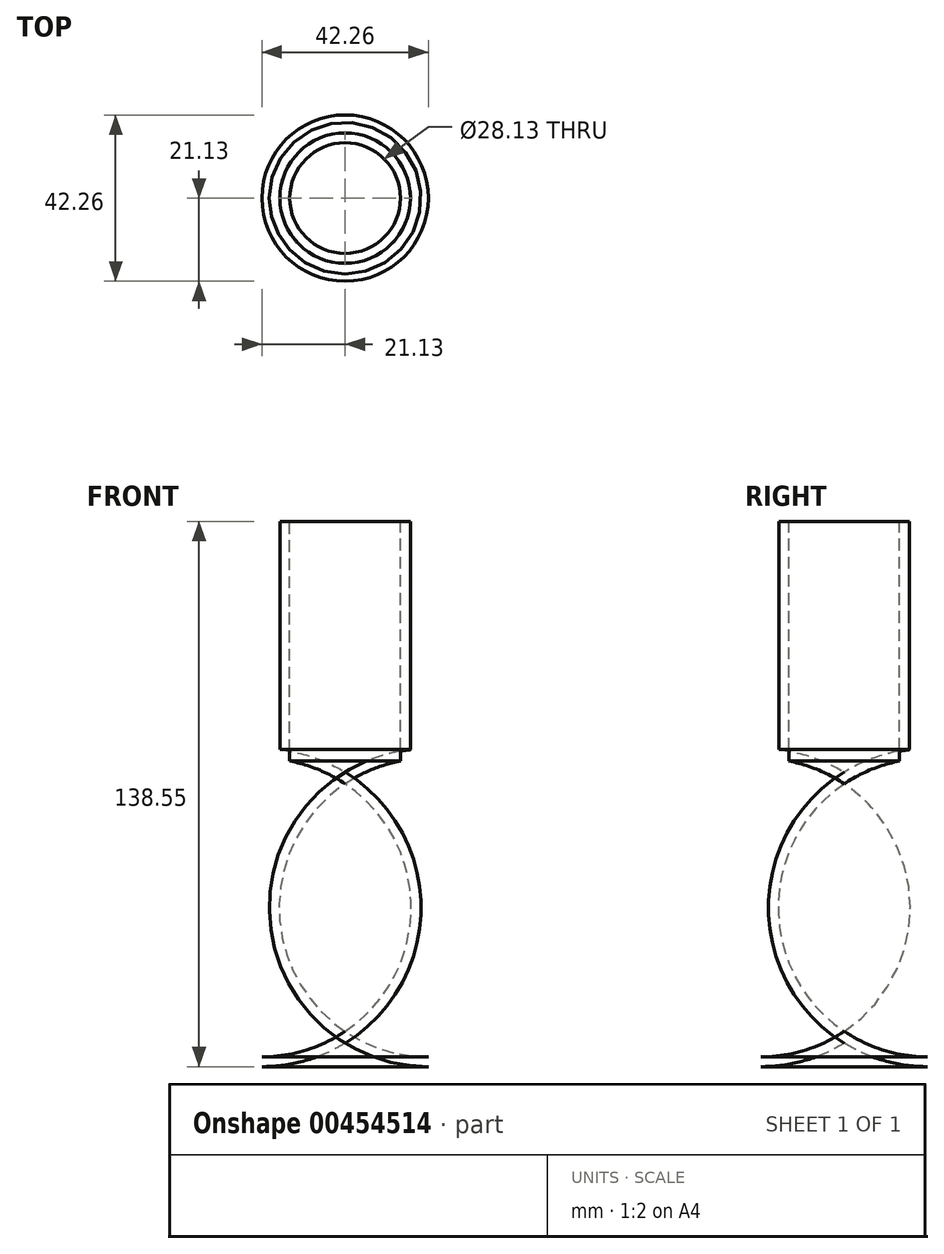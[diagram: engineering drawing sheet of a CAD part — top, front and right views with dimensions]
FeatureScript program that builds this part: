
annotation { "Feature Type Name" : "Feature", "Feature Type Description" : "" }
export const myFeature = defineFeature(function(context is Context, id is Id, definition is map)
    precondition{}
    {
        {
            var Q0;
            Q0=qCreatedBy(makeId("Front.planeOp"),FACE);
            var sketch = newSketch(context, id + "F0", { "sketchPlane" : qUnion([Q0])});
            skLineSegment(sketch, "E0", {"start": v(0, 70.82) * mm, "end": v(0, -67.97) * mm});
            skLineSegment(sketch, "E1", {"start": v(0, -67.97) * mm, "end": v(21.13, -67.97) * mm});
            skArc(sketch, "E2", {"start": v(21.13, -67.97) * mm, "mid": v(61.46, -25.28) * mm, "end": v(16.56, 12.57) * mm});
            skLineSegment(sketch, "E3", {"start": v(16.56, 12.57) * mm, "end": v(16.56, 70.54) * mm});
            skLineSegment(sketch, "E4", {"start": v(16.56, 70.54) * mm, "end": v(0, 70.82) * mm});
            skSolve(sketch);
        }
        {
            var Q0;
            Q0=makeQuery(id+"F0.imprint","IMPRINT",FACE,{"disambiguationData":[TD([[makeQuery(id+"F0.imprint","IMPRINT",EDGE,{"derivedFrom":sQuery(id+"F0.wireOp",EDGE,"E0")}),1.0]])]});
            var Q1;
            Q1=sQuery(id+"F0.wireOp",EDGE,"E0");
            revolve(context, id + "F1", {"entities" : qUnion([Q0]), "axis" : qUnion([Q1]), "revolveType" : RevolveType.FULL});
        }
        {
            var Q0;
            Q0=makeQuery(id+"F1.opRevolve","SWEPT_FACE",FACE,{"disambiguationData":[OSD([sQuery(id+"F0.wireOp",EDGE,"E4")])]});
            shell(context, id + "F2", {"entities" : qUnion([Q0]), "thickness" : 2.5 * mm});
        }
    });
